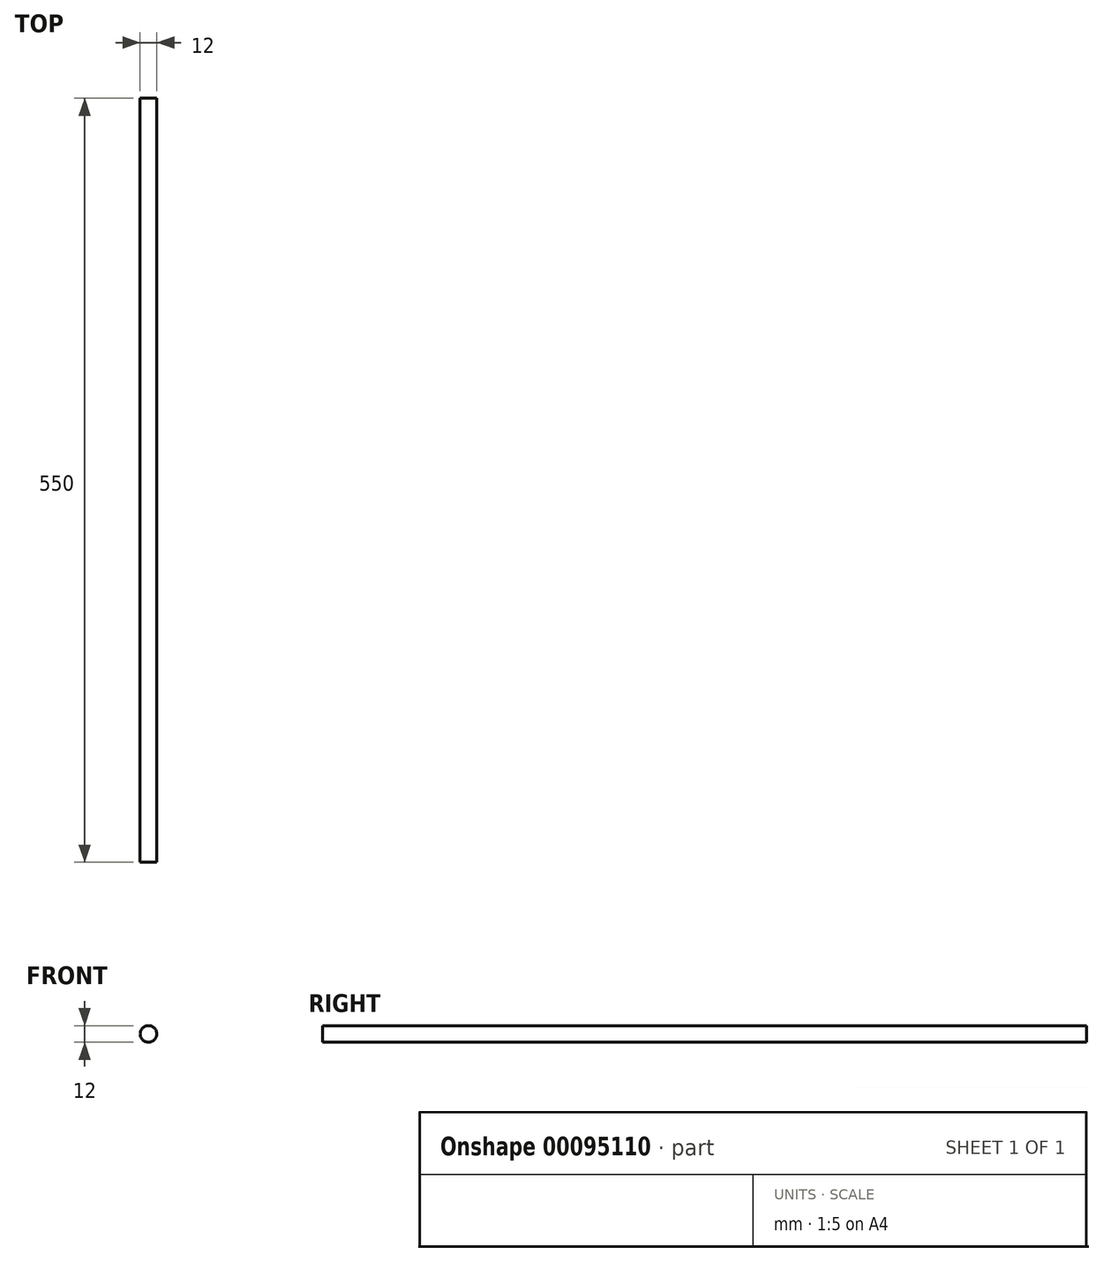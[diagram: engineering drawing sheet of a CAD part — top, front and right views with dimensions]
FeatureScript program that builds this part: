
annotation { "Feature Type Name" : "Feature", "Feature Type Description" : "" }
export const myFeature = defineFeature(function(context is Context, id is Id, definition is map)
    precondition{}
    {
        {
            var Q0;
            Q0=qCreatedBy(makeId("Front.planeOp"),FACE);
            var sketch = newSketch(context, id + "F0", { "sketchPlane" : qUnion([Q0])});
            skCircle(sketch, "E0", {"center": v(0, 0) * mm, "radius": 6 * mm});
            skSolve(sketch);
        }
        {
            var Q0;
            Q0 = qSketchRegion(id + "F0", true);
            var Q1;
            Q1=makeQuery(id+"F0.imprint","IMPRINT",FACE,{"disambiguationData":[TD([[makeQuery(id+"F0.imprint","IMPRINT",EDGE,{"derivedFrom":sQuery(id+"F0.wireOp",EDGE,"E0")}),1.0]])]});
            extrude(context, id + "F1", {"entities" : qUnion([Q0, Q1]), "oppositeDirection" : true, "depth" : 550 * mm});
        }
    });
